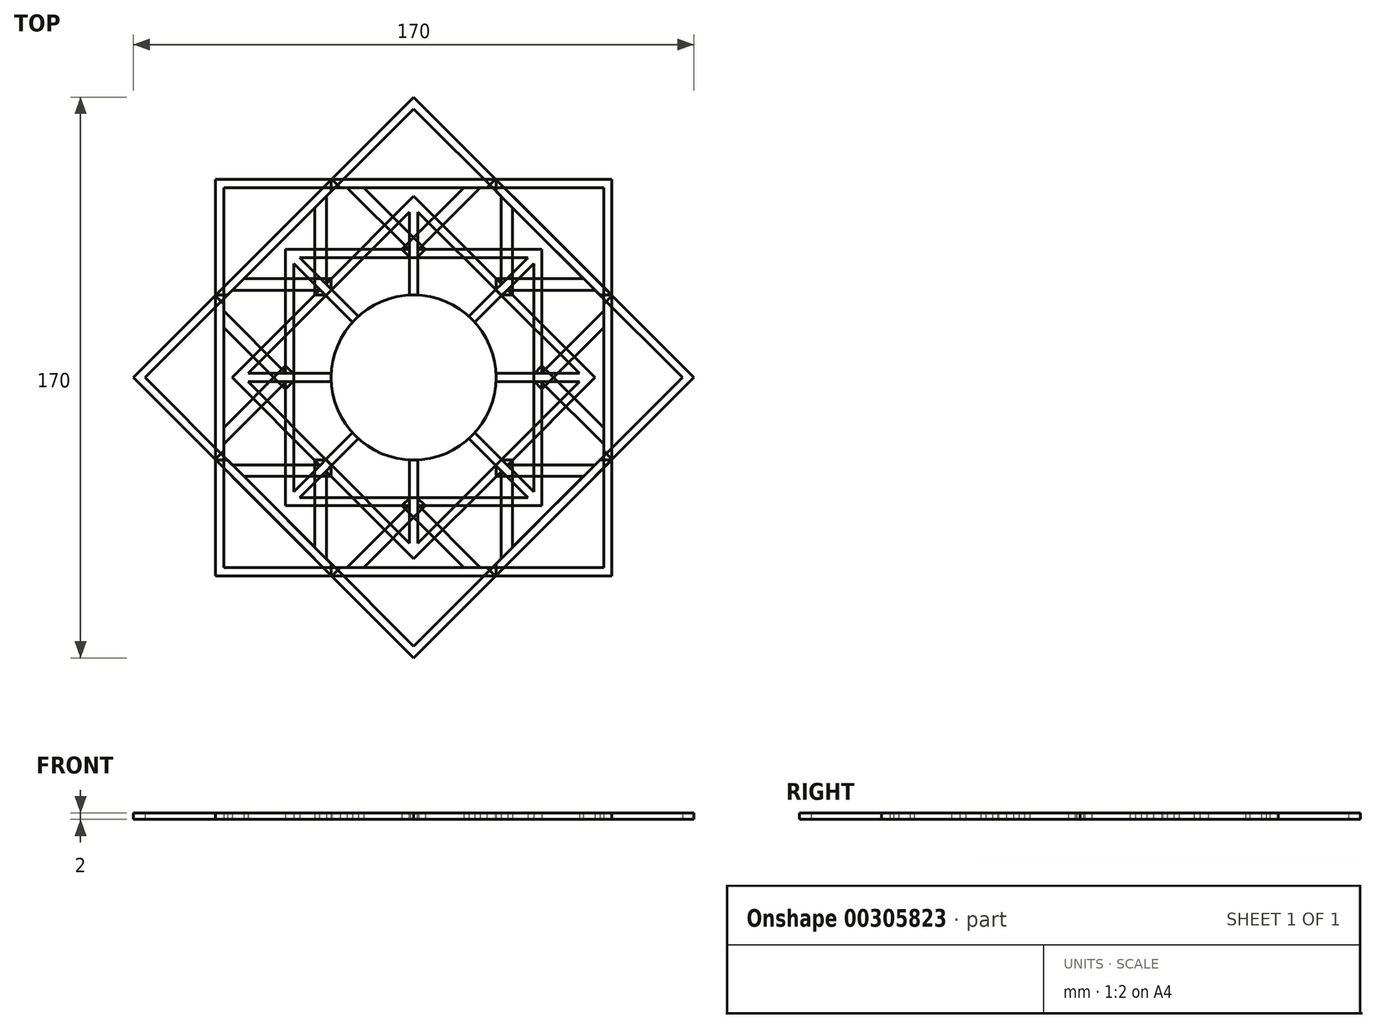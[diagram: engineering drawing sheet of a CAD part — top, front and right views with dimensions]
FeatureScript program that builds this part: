
annotation { "Feature Type Name" : "Feature", "Feature Type Description" : "" }
export const myFeature = defineFeature(function(context is Context, id is Id, definition is map)
    precondition{}
    {
        {
            var Q0;
            Q0=qCreatedBy(makeId("Top.planeOp"),FACE);
            var sketch = newSketch(context, id + "F0", { "sketchPlane" : qUnion([Q0])});
            skCircle(sketch, "E0", {"center": v(0, 0) * mm, "radius": 25 * mm});
            skLineSegment(sketch, "E1", {"start": v(0, 25) * mm, "end": v(0, 85) * mm});
            skLineSegment(sketch, "E2", {"start": v(0, 85) * mm, "end": v(-60, 25) * mm});
            skLineSegment(sketch, "E3", {"start": v(-60, 25) * mm, "end": v(0, 25) * mm});
            skLineSegment(sketch, "E4", {"start": v(0, 81.46) * mm, "end": v(-56.46, 25) * mm});
            skLineSegment(sketch, "E5.MirrorCS", {"start": v(0, 81.46) * mm, "end": v(56.46, 25) * mm});
            skLineSegment(sketch, "E6.MirrorCS", {"start": v(0, 85) * mm, "end": v(60, 25) * mm});
            skLineSegment(sketch, "E7.MirrorCS", {"start": v(60, 25) * mm, "end": v(0, 25) * mm});
            skLineSegment(sketch, "E8", {"start": v(0, 55) * mm, "end": v(-30, 25) * mm});
            skLineSegment(sketch, "E9", {"start": v(0, 51.46) * mm, "end": v(-26.46, 25) * mm});
            skLineSegment(sketch, "E10.MirrorCS", {"start": v(0, 51.46) * mm, "end": v(26.46, 25) * mm});
            skLineSegment(sketch, "E11.MirrorCS", {"start": v(0, 55) * mm, "end": v(30, 25) * mm});
            skLineSegment(sketch, "E12", {"start": v(-26.46, 25) * mm, "end": v(-26.46, 58.54) * mm});
            skLineSegment(sketch, "E13", {"start": v(-30, 25) * mm, "end": v(-30, 55) * mm});
            skLineSegment(sketch, "E14.MirrorCS", {"start": v(26.46, 25) * mm, "end": v(26.46, 58.54) * mm});
            skLineSegment(sketch, "E15.MirrorCS", {"start": v(30, 25) * mm, "end": v(30, 55) * mm});
            skLineSegment(sketch, "E16", {"start": v(-1.25, 50.21) * mm, "end": v(-1.25, 24.97) * mm});
            skLineSegment(sketch, "E17.MirrorCS", {"start": v(1.25, 50.21) * mm, "end": v(1.25, 24.97) * mm});
            skSolve(sketch);
        }
        {
            var Q0;
            {var subQ12=sQuery(id+"F0.wireOp",EDGE,"rgKxwHWQ-0tIm-QTML-jgtt-cgyoO9IEzFRk");Q0=makeQuery(id+"F0.imprint","IMPRINT",FACE,{"disambiguationData":[TD([[makeQuery(id+"F0.imprint","IMPRINT",EDGE,{"derivedFrom":subQ12}),-1.0]])]});}
            var Q1;
            {var subQ4=sQuery(id+"F0.wireOp",EDGE,"39eed24b-158e-49b0-9fed-3d602ac140780.MirrorCS");Q1=makeQuery(id+"F0.imprint","IMPRINT",FACE,{"disambiguationData":[TD([[makeQuery(id+"F0.imprint","IMPRINT",EDGE,{"derivedFrom":subQ4}),-1.0]])]});}
            var Q2;
            {var subQ0=sQuery(id+"F0.wireOp",EDGE,"39eed24b-158e-49b0-9fed-3d602ac140789.MirrorCS");var subQ3=sQuery(id+"F0.wireOp",EDGE,"39eed24b-158e-49b0-9fed-3d602ac1407812.MirrorCS");var subQ5=makeQuery(id+"F0.imprint","INTERSECT",VERTEX,{"derivedFrom":[subQ0,subQ3]});Q2=makeQuery(id+"F0.imprint","IMPRINT",FACE,{"disambiguationData":[TD([[makeQuery(id+"F0.imprint","IMPRINT",EDGE,{"disambiguationData":[TD([[subQ5,-1.0]])],"derivedFrom":subQ0}),1.0]])]});}
            var Q3;
            {var subQ0=sQuery(id+"F0.wireOp",EDGE,"t9s5LuAE-FJe1-1gRt-WiGv-LmA4uonB0Xpx");var subQ3=sQuery(id+"F0.wireOp",EDGE,"iTFk7IN0-3NO4-aDXI-xZCr-sOdiesEMgP7l");var subQ5=makeQuery(id+"F0.imprint","INTERSECT",VERTEX,{"derivedFrom":[subQ0,subQ3]});Q3=makeQuery(id+"F0.imprint","IMPRINT",FACE,{"disambiguationData":[TD([[makeQuery(id+"F0.imprint","IMPRINT",EDGE,{"disambiguationData":[TD([[subQ5,1.0]])],"derivedFrom":subQ0}),-1.0]])]});}
            var Q4;
            {var subQ0=sQuery(id+"F0.wireOp",EDGE,"39eed24b-158e-49b0-9fed-3d602ac1407810.MirrorCS");var subQ3=sQuery(id+"F0.wireOp",EDGE,"39eed24b-158e-49b0-9fed-3d602ac1407813.MirrorCS");var subQ5=makeQuery(id+"F0.imprint","INTERSECT",VERTEX,{"derivedFrom":[subQ0,subQ3]});Q4=makeQuery(id+"F0.imprint","IMPRINT",FACE,{"disambiguationData":[TD([[makeQuery(id+"F0.imprint","IMPRINT",EDGE,{"disambiguationData":[TD([[subQ5,-1.0]])],"derivedFrom":subQ0}),1.0]])]});}
            var Q5;
            {var subQ0=sQuery(id+"F0.wireOp",EDGE,"39eed24b-158e-49b0-9fed-3d602ac1407820.MirrorCS");var subQ3=sQuery(id+"F0.wireOp",EDGE,"39eed24b-158e-49b0-9fed-3d602ac1407821.MirrorCS");var subQ5=makeQuery(id+"F0.imprint","INTERSECT",VERTEX,{"derivedFrom":[subQ0,subQ3]});Q5=makeQuery(id+"F0.imprint","IMPRINT",FACE,{"disambiguationData":[TD([[makeQuery(id+"F0.imprint","IMPRINT",EDGE,{"disambiguationData":[TD([[subQ5,1.0]])],"derivedFrom":subQ0}),1.0]])]});}
            var Q6;
            {var subQ0=sQuery(id+"F0.wireOp",EDGE,"39eed24b-158e-49b0-9fed-3d602ac1407829.MirrorCS");var subQ3=sQuery(id+"F0.wireOp",EDGE,"39eed24b-158e-49b0-9fed-3d602ac1407818.MirrorCS");var subQ5=makeQuery(id+"F0.imprint","INTERSECT",VERTEX,{"derivedFrom":[subQ3,subQ0]});Q6=makeQuery(id+"F0.imprint","IMPRINT",FACE,{"disambiguationData":[TD([[makeQuery(id+"F0.imprint","IMPRINT",EDGE,{"disambiguationData":[TD([[subQ5,-1.0]])],"derivedFrom":subQ3}),-1.0]])]});}
            var Q7;
            {var subQ0=sQuery(id+"F0.wireOp",EDGE,"Dz0JH9oR-F1uf-Cc9M-qYLk-ZIQ6PCD5iHxu");var subQ3=sQuery(id+"F0.wireOp",EDGE,"z4HoAgif-IKVV-Kxpe-mfT6-CBQHM22fhQot");var subQ5=makeQuery(id+"F0.imprint","INTERSECT",VERTEX,{"derivedFrom":[subQ0,subQ3]});Q7=makeQuery(id+"F0.imprint","IMPRINT",FACE,{"disambiguationData":[TD([[makeQuery(id+"F0.imprint","IMPRINT",EDGE,{"disambiguationData":[TD([[subQ5,-1.0]])],"derivedFrom":subQ0}),-1.0]])]});}
            var Q8;
            {var subQ0=sQuery(id+"F0.wireOp",EDGE,"tcJsetix-ptgM-AA6w-ABbM-roNSNQ6rME7J");var subQ3=sQuery(id+"F0.wireOp",EDGE,"LPK1FYSa-4RyS-WpKL-8PT0-hAtOjgt3awO4");var subQ5=makeQuery(id+"F0.imprint","INTERSECT",VERTEX,{"derivedFrom":[subQ0,subQ3]});Q8=makeQuery(id+"F0.imprint","IMPRINT",FACE,{"disambiguationData":[TD([[makeQuery(id+"F0.imprint","IMPRINT",EDGE,{"disambiguationData":[TD([[subQ5,1.0]])],"derivedFrom":subQ0}),-1.0]])]});}
            var Q9;
            {var subQ0=sQuery(id+"F0.wireOp",EDGE,"BGNW9icz-v5DC-S9ia-8jwk-qwGL6yicAJM0");var subQ3=sQuery(id+"F0.wireOp",EDGE,"gKhBsrrR-tZhL-LkJv-gRrD-LfGJD4ry7Iq9");var subQ5=makeQuery(id+"F0.imprint","INTERSECT",VERTEX,{"derivedFrom":[subQ3,subQ0]});Q9=makeQuery(id+"F0.imprint","IMPRINT",FACE,{"disambiguationData":[TD([[makeQuery(id+"F0.imprint","IMPRINT",EDGE,{"disambiguationData":[TD([[subQ5,-1.0]])],"derivedFrom":subQ3}),-1.0]])]});}
            var Q10;
            {var subQ0=sQuery(id+"F0.wireOp",EDGE,"5KHXJwCu-BQyT-FO4B-sLiw-cAQWxpLxGazf");var subQ3=sQuery(id+"F0.wireOp",EDGE,"QsAnCMa8-trZm-cKtp-xhED-2LTobogKMZjS");var subQ5=makeQuery(id+"F0.imprint","INTERSECT",VERTEX,{"derivedFrom":[subQ3,subQ0]});Q10=makeQuery(id+"F0.imprint","IMPRINT",FACE,{"disambiguationData":[TD([[makeQuery(id+"F0.imprint","IMPRINT",EDGE,{"disambiguationData":[TD([[subQ5,-1.0]])],"derivedFrom":subQ3}),1.0]])]});}
            var Q11;
            {var subQ0=sQuery(id+"F0.wireOp",EDGE,"E7IZwEcp-4ycQ-N9yR-zE0W-1pGBjzpTROkv");var subQ3=sQuery(id+"F0.wireOp",EDGE,"j576JwIg-NamY-1qep-MOEI-4kHu3kVM2Hv1");var subQ5=makeQuery(id+"F0.imprint","INTERSECT",VERTEX,{"derivedFrom":[subQ0,subQ3]});Q11=makeQuery(id+"F0.imprint","IMPRINT",FACE,{"disambiguationData":[TD([[makeQuery(id+"F0.imprint","IMPRINT",EDGE,{"disambiguationData":[TD([[subQ5,1.0]])],"derivedFrom":subQ0}),1.0]])]});}
            var Q12;
            {var subQ0=sQuery(id+"F0.wireOp",EDGE,"jUmIYfnw-8Lwb-YlXg-2YpH-BOquHfJdh6lV");var subQ3=sQuery(id+"F0.wireOp",EDGE,"1l2XN7DS-QaV2-yNe4-gWKu-SUzt2v7CLsdl");var subQ5=makeQuery(id+"F0.imprint","INTERSECT",VERTEX,{"derivedFrom":[subQ0,subQ3]});Q12=makeQuery(id+"F0.imprint","IMPRINT",FACE,{"disambiguationData":[TD([[makeQuery(id+"F0.imprint","IMPRINT",EDGE,{"disambiguationData":[TD([[subQ5,-1.0]])],"derivedFrom":subQ0}),1.0]])]});}
            var Q13;
            {var subQ0=sQuery(id+"F0.wireOp",EDGE,"WclqcAAz-4p4y-WB3j-H9z4-ifuUmlISnmIe");var subQ3=sQuery(id+"F0.wireOp",EDGE,"GfKKvSQr-r8h9-oevS-bZHK-rX6XIx9WmUAn");var subQ5=makeQuery(id+"F0.imprint","INTERSECT",VERTEX,{"derivedFrom":[subQ0,subQ3]});Q13=makeQuery(id+"F0.imprint","IMPRINT",FACE,{"disambiguationData":[TD([[makeQuery(id+"F0.imprint","IMPRINT",EDGE,{"disambiguationData":[TD([[subQ5,1.0]])],"derivedFrom":subQ0}),1.0]])]});}
            var Q14;
            {var subQ0=sQuery(id+"F0.wireOp",EDGE,"39eed24b-158e-49b0-9fed-3d602ac1407814.MirrorCS");var subQ3=sQuery(id+"F0.wireOp",EDGE,"39eed24b-158e-49b0-9fed-3d602ac1407815.MirrorCS");var subQ5=makeQuery(id+"F0.imprint","INTERSECT",VERTEX,{"derivedFrom":[subQ0,subQ3]});Q14=makeQuery(id+"F0.imprint","IMPRINT",FACE,{"disambiguationData":[TD([[makeQuery(id+"F0.imprint","IMPRINT",EDGE,{"disambiguationData":[TD([[subQ5,-1.0]])],"derivedFrom":subQ0}),-1.0]])]});}
            var Q15;
            {var subQ0=sQuery(id+"F0.wireOp",EDGE,"39eed24b-158e-49b0-9fed-3d602ac1407816.MirrorCS");var subQ3=sQuery(id+"F0.wireOp",EDGE,"39eed24b-158e-49b0-9fed-3d602ac1407827.MirrorCS");var subQ5=makeQuery(id+"F0.imprint","INTERSECT",VERTEX,{"derivedFrom":[subQ0,subQ3]});Q15=makeQuery(id+"F0.imprint","IMPRINT",FACE,{"disambiguationData":[TD([[makeQuery(id+"F0.imprint","IMPRINT",EDGE,{"disambiguationData":[TD([[subQ5,-1.0]])],"derivedFrom":subQ0}),-1.0]])]});}
            var Q16;
            {var subQ0=sQuery(id+"F0.wireOp",EDGE,"39eed24b-158e-49b0-9fed-3d602ac1407817.MirrorCS");var subQ3=sQuery(id+"F0.wireOp",EDGE,"39eed24b-158e-49b0-9fed-3d602ac1407828.MirrorCS");var subQ5=makeQuery(id+"F0.imprint","INTERSECT",VERTEX,{"derivedFrom":[subQ0,subQ3]});Q16=makeQuery(id+"F0.imprint","IMPRINT",FACE,{"disambiguationData":[TD([[makeQuery(id+"F0.imprint","IMPRINT",EDGE,{"disambiguationData":[TD([[subQ5,1.0]])],"derivedFrom":subQ0}),-1.0]])]});}
            var Q17;
            {var subQ0=sQuery(id+"F0.wireOp",EDGE,"39eed24b-158e-49b0-9fed-3d602ac1407818.MirrorCS");var subQ3=sQuery(id+"F0.wireOp",EDGE,"39eed24b-158e-49b0-9fed-3d602ac1407829.MirrorCS");var subQ5=makeQuery(id+"F0.imprint","INTERSECT",VERTEX,{"derivedFrom":[subQ0,subQ3]});Q17=makeQuery(id+"F0.imprint","IMPRINT",FACE,{"disambiguationData":[TD([[makeQuery(id+"F0.imprint","IMPRINT",EDGE,{"disambiguationData":[TD([[subQ5,-1.0]])],"derivedFrom":subQ3}),1.0]])]});}
            var Q18;
            {var subQ0=sQuery(id+"F0.wireOp",EDGE,"39eed24b-158e-49b0-9fed-3d602ac1407821.MirrorCS");var subQ3=sQuery(id+"F0.wireOp",EDGE,"39eed24b-158e-49b0-9fed-3d602ac1407820.MirrorCS");var subQ5=makeQuery(id+"F0.imprint","INTERSECT",VERTEX,{"derivedFrom":[subQ3,subQ0]});Q18=makeQuery(id+"F0.imprint","IMPRINT",FACE,{"disambiguationData":[TD([[makeQuery(id+"F0.imprint","IMPRINT",EDGE,{"disambiguationData":[TD([[subQ5,-1.0]])],"derivedFrom":subQ3}),-1.0]])]});}
            var Q19;
            {var subQ0=sQuery(id+"F0.wireOp",EDGE,"39eed24b-158e-49b0-9fed-3d602ac1407817.MirrorCS");var subQ3=sQuery(id+"F0.wireOp",EDGE,"39eed24b-158e-49b0-9fed-3d602ac1407828.MirrorCS");var subQ5=makeQuery(id+"F0.imprint","INTERSECT",VERTEX,{"derivedFrom":[subQ0,subQ3]});Q19=makeQuery(id+"F0.imprint","IMPRINT",FACE,{"disambiguationData":[TD([[makeQuery(id+"F0.imprint","IMPRINT",EDGE,{"disambiguationData":[TD([[subQ5,-1.0]])],"derivedFrom":subQ0}),1.0]])]});}
            var Q20;
            {var subQ0=sQuery(id+"F0.wireOp",EDGE,"39eed24b-158e-49b0-9fed-3d602ac1407827.MirrorCS");var subQ3=sQuery(id+"F0.wireOp",EDGE,"39eed24b-158e-49b0-9fed-3d602ac1407816.MirrorCS");var subQ5=makeQuery(id+"F0.imprint","INTERSECT",VERTEX,{"derivedFrom":[subQ3,subQ0]});Q20=makeQuery(id+"F0.imprint","IMPRINT",FACE,{"disambiguationData":[TD([[makeQuery(id+"F0.imprint","IMPRINT",EDGE,{"disambiguationData":[TD([[subQ5,1.0]])],"derivedFrom":subQ3}),1.0]])]});}
            var Q21;
            {var subQ0=sQuery(id+"F0.wireOp",EDGE,"jUmIYfnw-8Lwb-YlXg-2YpH-BOquHfJdh6lV");var subQ3=sQuery(id+"F0.wireOp",EDGE,"1l2XN7DS-QaV2-yNe4-gWKu-SUzt2v7CLsdl");var subQ5=makeQuery(id+"F0.imprint","INTERSECT",VERTEX,{"derivedFrom":[subQ0,subQ3]});Q21=makeQuery(id+"F0.imprint","IMPRINT",FACE,{"disambiguationData":[TD([[makeQuery(id+"F0.imprint","IMPRINT",EDGE,{"disambiguationData":[TD([[subQ5,1.0]])],"derivedFrom":subQ0}),-1.0]])]});}
            var Q22;
            {var subQ0=sQuery(id+"F0.wireOp",EDGE,"E7IZwEcp-4ycQ-N9yR-zE0W-1pGBjzpTROkv");var subQ3=sQuery(id+"F0.wireOp",EDGE,"j576JwIg-NamY-1qep-MOEI-4kHu3kVM2Hv1");var subQ5=makeQuery(id+"F0.imprint","INTERSECT",VERTEX,{"derivedFrom":[subQ0,subQ3]});Q22=makeQuery(id+"F0.imprint","IMPRINT",FACE,{"disambiguationData":[TD([[makeQuery(id+"F0.imprint","IMPRINT",EDGE,{"disambiguationData":[TD([[subQ5,-1.0]])],"derivedFrom":subQ0}),-1.0]])]});}
            var Q23;
            {var subQ0=sQuery(id+"F0.wireOp",EDGE,"gKhBsrrR-tZhL-LkJv-gRrD-LfGJD4ry7Iq9");var subQ3=sQuery(id+"F0.wireOp",EDGE,"BGNW9icz-v5DC-S9ia-8jwk-qwGL6yicAJM0");var subQ5=makeQuery(id+"F0.imprint","INTERSECT",VERTEX,{"derivedFrom":[subQ0,subQ3]});Q23=makeQuery(id+"F0.imprint","IMPRINT",FACE,{"disambiguationData":[TD([[makeQuery(id+"F0.imprint","IMPRINT",EDGE,{"disambiguationData":[TD([[subQ5,-1.0]])],"derivedFrom":subQ3}),1.0]])]});}
            var Q24;
            {var subQ0=sQuery(id+"F0.wireOp",EDGE,"QsAnCMa8-trZm-cKtp-xhED-2LTobogKMZjS");var subQ3=sQuery(id+"F0.wireOp",EDGE,"5KHXJwCu-BQyT-FO4B-sLiw-cAQWxpLxGazf");var subQ5=makeQuery(id+"F0.imprint","INTERSECT",VERTEX,{"derivedFrom":[subQ0,subQ3]});Q24=makeQuery(id+"F0.imprint","IMPRINT",FACE,{"disambiguationData":[TD([[makeQuery(id+"F0.imprint","IMPRINT",EDGE,{"disambiguationData":[TD([[subQ5,-1.0]])],"derivedFrom":subQ3}),-1.0]])]});}
            var Q25;
            {var subQ0=sQuery(id+"F0.wireOp",EDGE,"39eed24b-158e-49b0-9fed-3d602ac1407810.MirrorCS");var subQ3=sQuery(id+"F0.wireOp",EDGE,"39eed24b-158e-49b0-9fed-3d602ac1407813.MirrorCS");var subQ5=makeQuery(id+"F0.imprint","INTERSECT",VERTEX,{"derivedFrom":[subQ0,subQ3]});Q25=makeQuery(id+"F0.imprint","IMPRINT",FACE,{"disambiguationData":[TD([[makeQuery(id+"F0.imprint","IMPRINT",EDGE,{"disambiguationData":[TD([[subQ5,1.0]])],"derivedFrom":subQ0}),-1.0]])]});}
            var Q26;
            {var subQ0=sQuery(id+"F0.wireOp",EDGE,"39eed24b-158e-49b0-9fed-3d602ac1407819.MirrorCS");var subQ3=sQuery(id+"F0.wireOp",EDGE,"39eed24b-158e-49b0-9fed-3d602ac1407824.MirrorCS");var subQ5=makeQuery(id+"F0.imprint","INTERSECT",VERTEX,{"derivedFrom":[subQ0,subQ3]});Q26=makeQuery(id+"F0.imprint","IMPRINT",FACE,{"disambiguationData":[TD([[makeQuery(id+"F0.imprint","IMPRINT",EDGE,{"disambiguationData":[TD([[subQ5,-1.0]])],"derivedFrom":subQ0}),-1.0]])]});}
            var Q27;
            {var subQ0=sQuery(id+"F0.wireOp",EDGE,"Dz0JH9oR-F1uf-Cc9M-qYLk-ZIQ6PCD5iHxu");var subQ3=sQuery(id+"F0.wireOp",EDGE,"z4HoAgif-IKVV-Kxpe-mfT6-CBQHM22fhQot");var subQ5=makeQuery(id+"F0.imprint","INTERSECT",VERTEX,{"derivedFrom":[subQ0,subQ3]});Q27=makeQuery(id+"F0.imprint","IMPRINT",FACE,{"disambiguationData":[TD([[makeQuery(id+"F0.imprint","IMPRINT",EDGE,{"disambiguationData":[TD([[subQ5,1.0]])],"derivedFrom":subQ0}),1.0]])]});}
            var Q28;
            {var subQ0=sQuery(id+"F0.wireOp",EDGE,"tcJsetix-ptgM-AA6w-ABbM-roNSNQ6rME7J");var subQ3=sQuery(id+"F0.wireOp",EDGE,"LPK1FYSa-4RyS-WpKL-8PT0-hAtOjgt3awO4");var subQ5=makeQuery(id+"F0.imprint","INTERSECT",VERTEX,{"derivedFrom":[subQ0,subQ3]});Q28=makeQuery(id+"F0.imprint","IMPRINT",FACE,{"disambiguationData":[TD([[makeQuery(id+"F0.imprint","IMPRINT",EDGE,{"disambiguationData":[TD([[subQ5,-1.0]])],"derivedFrom":subQ0}),1.0]])]});}
            var Q29;
            {var subQ3=sQuery(id+"F0.wireOp",EDGE,"39eed24b-158e-49b0-9fed-3d602ac140788.MirrorCS");Q29=makeQuery(id+"F0.imprint","IMPRINT",FACE,{"disambiguationData":[TD([[makeQuery(id+"F0.imprint","IMPRINT",EDGE,{"derivedFrom":subQ3}),1.0]])]});}
            var Q30;
            {var subQ3=sQuery(id+"F0.wireOp",EDGE,"Kxohg9qW-uOQq-93P6-tl5c-omxjy1Ke4CHe");Q30=makeQuery(id+"F0.imprint","IMPRINT",FACE,{"disambiguationData":[TD([[makeQuery(id+"F0.imprint","IMPRINT",EDGE,{"derivedFrom":subQ3}),-1.0]])]});}
            var Q31;
            {var subQ3=sQuery(id+"F0.wireOp",EDGE,"39eed24b-158e-49b0-9fed-3d602ac1407811.MirrorCS");Q31=makeQuery(id+"F0.imprint","IMPRINT",FACE,{"disambiguationData":[TD([[makeQuery(id+"F0.imprint","IMPRINT",EDGE,{"derivedFrom":subQ3}),-1.0]])]});}
            var Q32;
            {var subQ3=sQuery(id+"F0.wireOp",EDGE,"zhDcuXVF-Ki8l-OoJ5-r1cu-Qsn10oomHP4L");Q32=makeQuery(id+"F0.imprint","IMPRINT",FACE,{"disambiguationData":[TD([[makeQuery(id+"F0.imprint","IMPRINT",EDGE,{"derivedFrom":subQ3}),1.0]])]});}
            var Q33;
            {var subQ3=sQuery(id+"F0.wireOp",EDGE,"39eed24b-158e-49b0-9fed-3d602ac1407815.MirrorCS");var subQ5=sQuery(id+"F0.wireOp",EDGE,"39eed24b-158e-49b0-9fed-3d602ac1407814.MirrorCS");var subQ7=makeQuery(id+"F0.imprint","INTERSECT",VERTEX,{"derivedFrom":[subQ5,subQ3]});Q33=makeQuery(id+"F0.imprint","IMPRINT",FACE,{"disambiguationData":[TD([[makeQuery(id+"F0.imprint","IMPRINT",EDGE,{"disambiguationData":[TD([[subQ7,1.0]])],"derivedFrom":subQ5}),1.0]])]});}
            var Q34;
            {var subQ3=sQuery(id+"F0.wireOp",EDGE,"WclqcAAz-4p4y-WB3j-H9z4-ifuUmlISnmIe");var subQ5=sQuery(id+"F0.wireOp",EDGE,"GfKKvSQr-r8h9-oevS-bZHK-rX6XIx9WmUAn");var subQ7=makeQuery(id+"F0.imprint","INTERSECT",VERTEX,{"derivedFrom":[subQ3,subQ5]});Q34=makeQuery(id+"F0.imprint","IMPRINT",FACE,{"disambiguationData":[TD([[makeQuery(id+"F0.imprint","IMPRINT",EDGE,{"disambiguationData":[TD([[subQ7,-1.0]])],"derivedFrom":subQ3}),-1.0]])]});}
            var Q35;
            {var subQ3=sQuery(id+"F0.wireOp",EDGE,"t9s5LuAE-FJe1-1gRt-WiGv-LmA4uonB0Xpx");var subQ5=sQuery(id+"F0.wireOp",EDGE,"iTFk7IN0-3NO4-aDXI-xZCr-sOdiesEMgP7l");var subQ6=makeQuery(id+"F0.imprint","INTERSECT",VERTEX,{"derivedFrom":[subQ3,subQ5]});Q35=makeQuery(id+"F0.imprint","IMPRINT",FACE,{"disambiguationData":[TD([[makeQuery(id+"F0.imprint","IMPRINT",EDGE,{"disambiguationData":[TD([[subQ6,-1.0]])],"derivedFrom":subQ3}),1.0]])]});}
            var Q36;
            {var subQ3=sQuery(id+"F0.wireOp",EDGE,"39eed24b-158e-49b0-9fed-3d602ac1407812.MirrorCS");var subQ5=sQuery(id+"F0.wireOp",EDGE,"39eed24b-158e-49b0-9fed-3d602ac140789.MirrorCS");var subQ7=makeQuery(id+"F0.imprint","INTERSECT",VERTEX,{"derivedFrom":[subQ5,subQ3]});Q36=makeQuery(id+"F0.imprint","IMPRINT",FACE,{"disambiguationData":[TD([[makeQuery(id+"F0.imprint","IMPRINT",EDGE,{"disambiguationData":[TD([[subQ7,1.0]])],"derivedFrom":subQ5}),-1.0]])]});}
            var Q37;
            {var subQ2=sQuery(id+"F0.wireOp",EDGE,"E5.MirrorCS");Q37=makeQuery(id+"F0.imprint","IMPRINT",FACE,{"disambiguationData":[TD([[makeQuery(id+"F0.imprint","IMPRINT",EDGE,{"derivedFrom":subQ2}),1.0]])]});}
            var Q38;
            {var subQ0=sQuery(id+"F0.wireOp",EDGE,"E2");Q38=makeQuery(id+"F0.imprint","IMPRINT",FACE,{"disambiguationData":[TD([[makeQuery(id+"F0.imprint","IMPRINT",EDGE,{"derivedFrom":subQ0}),1.0]])]});}
            var Q39;
            {var subQ0=sQuery(id+"F0.wireOp",EDGE,"E8");Q39=makeQuery(id+"F0.imprint","IMPRINT",FACE,{"disambiguationData":[TD([[makeQuery(id+"F0.imprint","IMPRINT",EDGE,{"derivedFrom":subQ0}),1.0]])]});}
            var Q40;
            {var subQ2=sQuery(id+"F0.wireOp",EDGE,"E10.MirrorCS");Q40=makeQuery(id+"F0.imprint","IMPRINT",FACE,{"disambiguationData":[TD([[makeQuery(id+"F0.imprint","IMPRINT",EDGE,{"derivedFrom":subQ2}),1.0]])]});}
            var Q41;
            {var subQ0=sQuery(id+"F0.wireOp",EDGE,"E12");var subQ1=sQuery(id+"F0.wireOp",EDGE,"E4");var subQ2=makeQuery(id+"F0.imprint","INTERSECT",VERTEX,{"derivedFrom":[subQ1,subQ0]});Q41=makeQuery(id+"F0.imprint","IMPRINT",FACE,{"disambiguationData":[TD([[makeQuery(id+"F0.imprint","IMPRINT",EDGE,{"disambiguationData":[TD([[subQ2,-1.0]])],"derivedFrom":subQ1}),1.0]])]});}
            var Q42;
            {var subQ3=sQuery(id+"F0.wireOp",EDGE,"E9");Q42=makeQuery(id+"F0.imprint","IMPRINT",FACE,{"disambiguationData":[TD([[makeQuery(id+"F0.imprint","IMPRINT",EDGE,{"derivedFrom":subQ3}),-1.0]])]});}
            var Q43;
            {var subQ0=sQuery(id+"F0.wireOp",EDGE,"E14.MirrorCS");var subQ3=sQuery(id+"F0.wireOp",EDGE,"E11.MirrorCS");var subQ5=makeQuery(id+"F0.imprint","INTERSECT",VERTEX,{"derivedFrom":[subQ3,subQ0]});Q43=makeQuery(id+"F0.imprint","IMPRINT",FACE,{"disambiguationData":[TD([[makeQuery(id+"F0.imprint","IMPRINT",EDGE,{"disambiguationData":[TD([[subQ5,-1.0]])],"derivedFrom":subQ3}),-1.0]])]});}
            var Q44;
            {var subQ0=sQuery(id+"F0.wireOp",EDGE,"E14.MirrorCS");var subQ1=sQuery(id+"F0.wireOp",EDGE,"E5.MirrorCS");var subQ2=makeQuery(id+"F0.imprint","INTERSECT",VERTEX,{"derivedFrom":[subQ1,subQ0]});Q44=makeQuery(id+"F0.imprint","IMPRINT",FACE,{"disambiguationData":[TD([[makeQuery(id+"F0.imprint","IMPRINT",EDGE,{"disambiguationData":[TD([[subQ2,-1.0]])],"derivedFrom":subQ1}),-1.0]])]});}
            var Q45;
            Q45=makeQuery(id+"F0.imprint","IMPRINT",FACE,{"disambiguationData":[TD([[makeQuery(id+"F0.imprint","IMPRINT",EDGE,{"derivedFrom":sQuery(id+"F0.wireOp",EDGE,"E0")}),1.0]])]});
            var Q46;
            {var subQ3=sQuery(id+"F0.wireOp",EDGE,"E10.MirrorCS");var subQ5=sQuery(id+"F0.wireOp",EDGE,"E17.MirrorCS");var subQ7=makeQuery(id+"F0.imprint","INTERSECT",VERTEX,{"derivedFrom":[subQ3,subQ5]});Q46=makeQuery(id+"F0.imprint","IMPRINT",FACE,{"disambiguationData":[TD([[makeQuery(id+"F0.imprint","IMPRINT",EDGE,{"disambiguationData":[TD([[subQ7,-1.0]])],"derivedFrom":subQ5}),-1.0]])]});}
            var Q47;
            {var subQ3=sQuery(id+"F0.wireOp",EDGE,"E9");var subQ5=sQuery(id+"F0.wireOp",EDGE,"E16");var subQ7=makeQuery(id+"F0.imprint","INTERSECT",VERTEX,{"derivedFrom":[subQ3,subQ5]});Q47=makeQuery(id+"F0.imprint","IMPRINT",FACE,{"disambiguationData":[TD([[makeQuery(id+"F0.imprint","IMPRINT",EDGE,{"disambiguationData":[TD([[subQ7,-1.0]])],"derivedFrom":subQ5}),1.0]])]});}
            extrude(context, id + "F1", {"entities" : qUnion([Q0, Q1, Q2, Q3, Q4, Q5, Q6, Q7, Q8, Q9, Q10, Q11, Q12, Q13, Q14, Q15, Q16, Q17, Q18, Q19, Q20, Q21, Q22, Q23, Q24, Q25, Q26, Q27, Q28, Q29, Q30, Q31, Q32, Q33, Q34, Q35, Q36, Q37, Q38, Q39, Q40, Q41, Q42, Q43, Q44, Q45, Q46, Q47]), "depth" : 2 * mm});
        }
        {
            var Q0;
            Q0=qCreatedBy(makeId("Right.planeOp"),FACE);
            var sketch = newSketch(context, id + "F2", { "sketchPlane" : qUnion([Q0])});
            skLineSegment(sketch, "E18", {"start": v(0, 0) * mm, "end": v(0, 32.34) * mm});
            skSolve(sketch);
        }
        {
            var Q0;
            Q0=makeQuery(id+"F1.opExtrude","SWEPT_BODY",BODY,{"disambiguationData":[OSD([sQuery(id+"F0.wireOp",EDGE,"E2"),sQuery(id+"F0.wireOp",EDGE,"E3"),sQuery(id+"F0.wireOp",EDGE,"E4"),sQuery(id+"F0.wireOp",EDGE,"E5.MirrorCS"),sQuery(id+"F0.wireOp",EDGE,"E6.MirrorCS"),sQuery(id+"F0.wireOp",EDGE,"E7.MirrorCS")])]});
            var Q1;
            Q1=makeQuery(id+"F1.opExtrude","SWEPT_BODY",BODY,{"disambiguationData":[OSD([sQuery(id+"F0.wireOp",EDGE,"E3"),sQuery(id+"F0.wireOp",EDGE,"E7.MirrorCS"),sQuery(id+"F0.wireOp",EDGE,"E8"),sQuery(id+"F0.wireOp",EDGE,"E9"),sQuery(id+"F0.wireOp",EDGE,"E10.MirrorCS"),sQuery(id+"F0.wireOp",EDGE,"E11.MirrorCS")])]});
            var Q2;
            Q2=sQuery(id+"F2.wireOp",EDGE,"E18");
            circularPattern(context, id + "F3", {"entities" : qUnion([Q0, Q1]), "axis" : qUnion([Q2]), "angle" : 360 * degree, "instanceCount" : 8, "equalSpace" : true});
        }
    });
